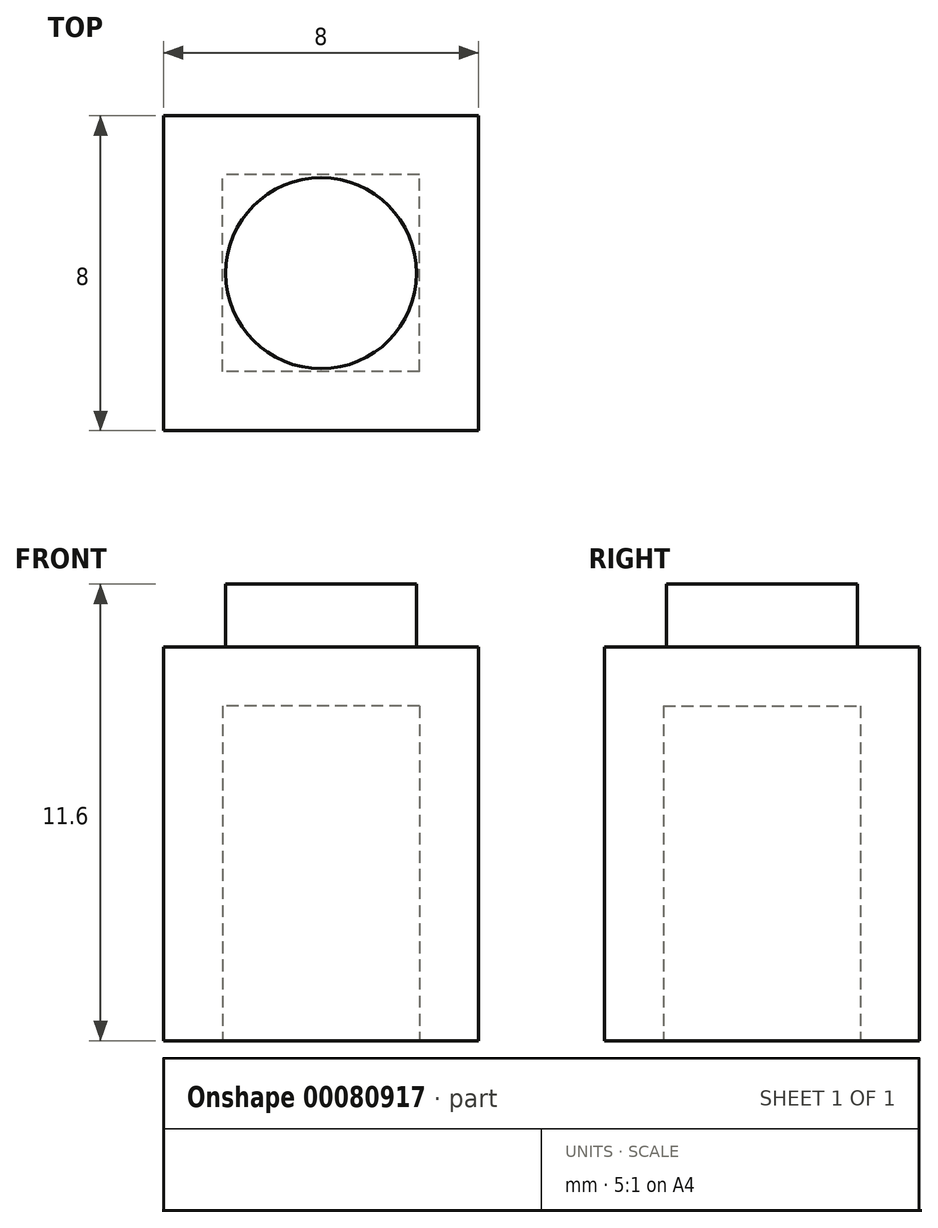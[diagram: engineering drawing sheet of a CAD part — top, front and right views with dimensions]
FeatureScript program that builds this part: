
annotation { "Feature Type Name" : "Feature", "Feature Type Description" : "" }
export const myFeature = defineFeature(function(context is Context, id is Id, definition is map)
    precondition{}
    {
        {
            var Q0;
            Q0=qCreatedBy(makeId("Top.planeOp"),FACE);
            var sketch = newSketch(context, id + "F0", { "sketchPlane" : qUnion([Q0])});
            skLineSegment(sketch, "E0.bottom", {"start": v(4, -4) * mm, "end": v(-4, -4) * mm});
            skLineSegment(sketch, "E0.top", {"start": v(4, 4) * mm, "end": v(-4, 4) * mm});
            skLineSegment(sketch, "E0.left", {"start": v(4, -4) * mm, "end": v(4, 4) * mm});
            skLineSegment(sketch, "E0.right", {"start": v(-4, -4) * mm, "end": v(-4, 4) * mm});
            skPoint(sketch, "E0.middle", {"position": v(0, 0) * mm});
            skSolve(sketch);
        }
        {
            var Q0;
            Q0 = qSketchRegion(id + "F0", true);
            extrude(context, id + "F1", {"entities" : qUnion([Q0]), "depth" : 10 * mm});
        }
        {
            var Q0;
            Q0=makeQuery(id+"F1.opExtrude","CAP_FACE",FACE,{"disambiguationData":[OSD([sQuery(id+"F0.wireOp",EDGE,"E0.bottom"),sQuery(id+"F0.wireOp",EDGE,"E0.top"),sQuery(id+"F0.wireOp",EDGE,"E0.left"),sQuery(id+"F0.wireOp",EDGE,"E0.right")])],"isStart":true});
            shell(context, id + "F2", {"entities" : qUnion([Q0]), "thickness" : 1.5 * mm});
        }
        {
            var Q0;
            Q0=makeQuery(id+"F1.opExtrude","CAP_FACE",FACE,{"disambiguationData":[OSD([sQuery(id+"F0.wireOp",EDGE,"E0.bottom"),sQuery(id+"F0.wireOp",EDGE,"E0.top"),sQuery(id+"F0.wireOp",EDGE,"E0.left"),sQuery(id+"F0.wireOp",EDGE,"E0.right")])],"isStart":false});
            var sketch = newSketch(context, id + "F3", { "sketchPlane" : qUnion([Q0])});
            skCircle(sketch, "E1", {"center": v(0, 0) * mm, "radius": 2.43 * mm});
            skSolve(sketch);
        }
        {
            var Q0;
            Q0 = qSketchRegion(id + "F3", true);
            extrude(context, id + "F4", {"entities" : qUnion([Q0]), "operationType" : NewBodyOperationType.ADD, "depth" : 1.6 * mm});
        }
    });
